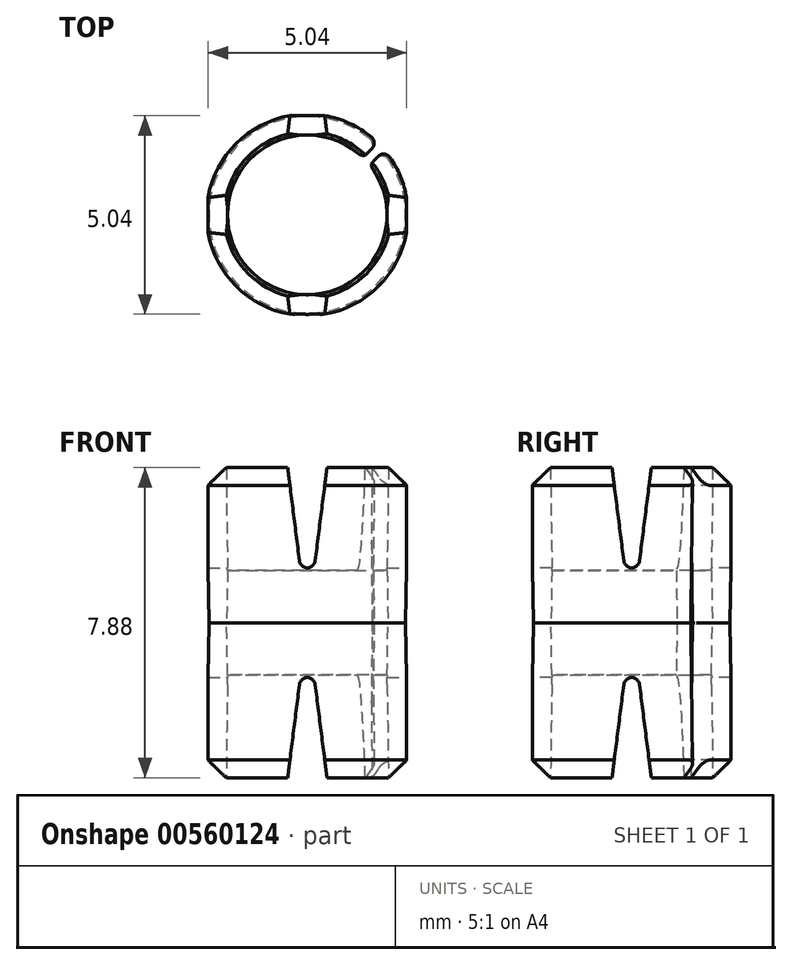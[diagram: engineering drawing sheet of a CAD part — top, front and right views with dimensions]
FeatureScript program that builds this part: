
annotation { "Feature Type Name" : "Feature", "Feature Type Description" : "" }
export const myFeature = defineFeature(function(context is Context, id is Id, definition is map)
    precondition{}
    {
        {
            var Q0;
            Q0=qCreatedBy(makeId("Top.planeOp"),FACE);
            var sketch = newSketch(context, id + "F0", { "sketchPlane" : qUnion([Q0])});
            skCircle(sketch, "E0", {"center": v(0, 0) * mm, "radius": 2.5 * mm});
            skCircle(sketch, "E1", {"center": v(0, 0) * mm, "radius": 2.05 * mm});
            skSolve(sketch);
        }
        {
            var Q0;
            Q0 = qSketchRegion(id + "F0", true);
            extrude(context, id + "F1", {"entities" : qUnion([Q0]), "depth" : 4 * mm, "offsetDistance" : 25 * mm, "hasDraft" : true, "draftAngle" : 1 * degree, "hasSecondDirection" : true, "secondDirectionOppositeDirection" : true, "secondDirectionDepth" : 4 * mm, "hasSecondDirectionDraft" : true, "secondDirectionDraftAngle" : 1 * degree});
        }
        {
            var Q0;
            Q0=qCreatedBy(makeId("Top.planeOp"),FACE);
            var sketch = newSketch(context, id + "F2", { "sketchPlane" : qUnion([Q0])});
            skCircle(sketch, "E2", {"center": v(0, 0) * mm, "radius": 1.98 * mm});
            skSolve(sketch);
        }
        {
            var Q0;
            Q0 = qSketchRegion(id + "F2", true);
            extrude(context, id + "F3", {"entities" : qUnion([Q0]), "operationType" : NewBodyOperationType.REMOVE, "endBound" : BoundingType.SYMMETRIC, "oppositeDirection" : true, "depth" : 50 * mm, "offsetDistance" : 25 * mm, "hasDraft" : true, "draftAngle" : 2 * degree});
        }
        {
            var Q0;
            Q0=makeQuery(id+"F1.opExtrude","CAP_EDGE",EDGE,{"disambiguationData":[OSD([sQuery(id+"F0.wireOp",EDGE,"E0")])],"isStart":false});
            var Q1;
            Q1=makeQuery(id+"F1.opExtrude","CAP_EDGE",EDGE,{"disambiguationData":[OSD([sQuery(id+"F0.wireOp",EDGE,"E0")])],"isStart":true});
            chamfer(context, id + "F4", {"entities" : qUnion([Q0, Q1]), "width" : 0.5 * mm, "tangentPropagation" : true});
        }
        {
            var Q0;
            Q0=qCreatedBy(makeId("Right.planeOp"),FACE);
            var sketch = newSketch(context, id + "F5", { "sketchPlane" : qUnion([Q0])});
            skLineSegment(sketch, "E3", {"start": v(0.2, -1.57) * mm, "end": v(0.5, -3.95) * mm});
            skLineSegment(sketch, "E4", {"start": v(0.5, -3.95) * mm, "end": v(-0.5, -3.95) * mm});
            skLineSegment(sketch, "E5", {"start": v(-0.5, -3.95) * mm, "end": v(-0.2, -1.57) * mm});
            skPoint(sketch, "E6.visualSharp", {"position": v(0, 0) * mm});
            skArc(sketch, "E6.filletArc", {"start": v(0.2, -1.57) * mm, "mid": v(0, -1.4) * mm, "end": v(-0.2, -1.57) * mm});
            skArc(sketch, "E7.MirrorCS", {"start": v(0.2, 1.57) * mm, "mid": v(0, 1.4) * mm, "end": v(-0.2, 1.57) * mm});
            skLineSegment(sketch, "E8.MirrorCS", {"start": v(0.2, 1.57) * mm, "end": v(0.5, 3.95) * mm});
            skLineSegment(sketch, "E9.MirrorCS", {"start": v(0.5, 3.95) * mm, "end": v(-0.5, 3.95) * mm});
            skLineSegment(sketch, "E10.MirrorCS", {"start": v(-0.5, 3.95) * mm, "end": v(-0.2, 1.57) * mm});
            skSolve(sketch);
        }
        {
            var Q0;
            Q0 = qSketchRegion(id + "F5", true);
            extrude(context, id + "F6", {"entities" : qUnion([Q0]), "operationType" : NewBodyOperationType.REMOVE, "oppositeDirection" : true, "depth" : 25 * mm, "offsetDistance" : 25 * mm, "hasSecondDirection" : true, "secondDirectionOppositeDirection" : false, "secondDirectionDepth" : 25 * mm});
        }
        {
            var Q0;
            Q0=qCreatedBy(makeId("Front.planeOp"),FACE);
            var sketch = newSketch(context, id + "F7", { "sketchPlane" : qUnion([Q0])});
            skLineSegment(sketch, "E11", {"start": v(0.2, -1.57) * mm, "end": v(0.5, -3.95) * mm});
            skLineSegment(sketch, "E12", {"start": v(0.5, -3.95) * mm, "end": v(-0.5, -3.95) * mm});
            skLineSegment(sketch, "E13", {"start": v(-0.5, -3.95) * mm, "end": v(-0.2, -1.57) * mm});
            skPoint(sketch, "E14.visualSharp", {"position": v(0, 0) * mm});
            skArc(sketch, "E14.filletArc", {"start": v(0.2, -1.57) * mm, "mid": v(0, -1.4) * mm, "end": v(-0.2, -1.57) * mm});
            skArc(sketch, "E15.MirrorCS", {"start": v(0.2, 1.57) * mm, "mid": v(0, 1.4) * mm, "end": v(-0.2, 1.57) * mm});
            skLineSegment(sketch, "E16.MirrorCS", {"start": v(0.2, 1.57) * mm, "end": v(0.5, 3.95) * mm});
            skLineSegment(sketch, "E17.MirrorCS", {"start": v(0.5, 3.95) * mm, "end": v(-0.5, 3.95) * mm});
            skLineSegment(sketch, "E18.MirrorCS", {"start": v(-0.5, 3.95) * mm, "end": v(-0.2, 1.57) * mm});
            skSolve(sketch);
        }
        {
            var Q0;
            Q0 = qSketchRegion(id + "F7", true);
            extrude(context, id + "F8", {"entities" : qUnion([Q0]), "operationType" : NewBodyOperationType.REMOVE, "oppositeDirection" : true, "depth" : 25 * mm, "offsetDistance" : 25 * mm, "hasSecondDirection" : true, "secondDirectionOppositeDirection" : false, "secondDirectionDepth" : 25 * mm});
        }
        {
            var Q0;
            Q0=qCreatedBy(makeId("Top.planeOp"),FACE);
            var sketch = newSketch(context, id + "F9", { "sketchPlane" : qUnion([Q0])});
            skLineSegment(sketch, "E19", {"start": v(0, 0) * mm, "end": v(3.4, 3.48) * mm});
            skLineSegment(sketch, "E20", {"start": v(3.4, 3.48) * mm, "end": v(3.57, 3.3) * mm});
            skLineSegment(sketch, "E21", {"start": v(3.57, 3.3) * mm, "end": v(0.56, 0.22) * mm});
            skLineSegment(sketch, "E22", {"start": v(0.56, 0.22) * mm, "end": v(0, 0) * mm});
            skSolve(sketch);
        }
        {
            var Q0;
            Q0=makeQuery(id+"F9.imprint","IMPRINT",FACE,{"disambiguationData":[TD([[makeQuery(id+"F9.imprint","IMPRINT",EDGE,{"derivedFrom":sQuery(id+"F9.wireOp",EDGE,"E19")}),-1.0]])]});
            extrude(context, id + "F10", {"entities" : qUnion([Q0]), "operationType" : NewBodyOperationType.REMOVE, "depth" : 25 * mm, "offsetDistance" : 25 * mm, "hasSecondDirection" : true, "secondDirectionOppositeDirection" : true, "secondDirectionDepth" : 25 * mm});
        }
        {
            var Q0;
            Q0=makeQuery(id+"F10.boolean.opBoolean","INTERSECT",EDGE,{"derivedFrom":[makeQuery(id+"F1.*.split.splitOp","SPLIT",FACE,{"derivedFrom":makeQuery(id+"F1.opExtrude","SWEPT_FACE",FACE,{"disambiguationData":[OSD([sQuery(id+"F0.wireOp",EDGE,"E1")])]})}),makeQuery(id+"F10.opExtrude","SWEPT_FACE",FACE,{"disambiguationData":[OSD([sQuery(id+"F9.wireOp",EDGE,"E19")])]})]});
            var Q1;
            Q1=makeQuery(id+"F10.boolean.opBoolean","INTERSECT",EDGE,{"derivedFrom":[makeQuery(id+"F1.*.split.splitOp","SPLIT",FACE,{"derivedFrom":makeQuery(id+"F1.opExtrude","SWEPT_FACE",FACE,{"disambiguationData":[OSD([sQuery(id+"F0.wireOp",EDGE,"E1")])]}),"isFromBackBody":true}),makeQuery(id+"F10.opExtrude","SWEPT_FACE",FACE,{"disambiguationData":[OSD([sQuery(id+"F9.wireOp",EDGE,"E19")])]})]});
            var Q2;
            Q2=makeQuery(id+"F10.boolean.opBoolean","INTERSECT",EDGE,{"derivedFrom":[makeQuery(id+"F1.*.split.splitOp","SPLIT",FACE,{"derivedFrom":makeQuery(id+"F1.opExtrude","SWEPT_FACE",FACE,{"disambiguationData":[OSD([sQuery(id+"F0.wireOp",EDGE,"E1")])]}),"isFromBackBody":true}),makeQuery(id+"F10.opExtrude","SWEPT_FACE",FACE,{"disambiguationData":[OSD([sQuery(id+"F9.wireOp",EDGE,"E21")])]})]});
            var Q3;
            Q3=makeQuery(id+"F10.boolean.opBoolean","INTERSECT",EDGE,{"derivedFrom":[makeQuery(id+"F1.*.split.splitOp","SPLIT",FACE,{"derivedFrom":makeQuery(id+"F1.opExtrude","SWEPT_FACE",FACE,{"disambiguationData":[OSD([sQuery(id+"F0.wireOp",EDGE,"E1")])]})}),makeQuery(id+"F10.opExtrude","SWEPT_FACE",FACE,{"disambiguationData":[OSD([sQuery(id+"F9.wireOp",EDGE,"E21")])]})]});
            var Q4;
            Q4=makeQuery(id+"F10.boolean.opBoolean","INTERSECT",EDGE,{"derivedFrom":[makeQuery(id+"F1.*.split.splitOp","SPLIT",FACE,{"derivedFrom":makeQuery(id+"F1.opExtrude","SWEPT_FACE",FACE,{"disambiguationData":[OSD([sQuery(id+"F0.wireOp",EDGE,"E0")])]}),"isFromBackBody":true}),makeQuery(id+"F10.opExtrude","SWEPT_FACE",FACE,{"disambiguationData":[OSD([sQuery(id+"F9.wireOp",EDGE,"E21")])]})]});
            var Q5;
            Q5=makeQuery(id+"F10.boolean.opBoolean","INTERSECT",EDGE,{"derivedFrom":[makeQuery(id+"F1.*.split.splitOp","SPLIT",FACE,{"derivedFrom":makeQuery(id+"F1.opExtrude","SWEPT_FACE",FACE,{"disambiguationData":[OSD([sQuery(id+"F0.wireOp",EDGE,"E0")])]})}),makeQuery(id+"F10.opExtrude","SWEPT_FACE",FACE,{"disambiguationData":[OSD([sQuery(id+"F9.wireOp",EDGE,"E21")])]})]});
            var Q6;
            Q6=makeQuery(id+"F10.boolean.opBoolean","INTERSECT",EDGE,{"derivedFrom":[makeQuery(id+"F1.*.split.splitOp","SPLIT",FACE,{"derivedFrom":makeQuery(id+"F1.opExtrude","SWEPT_FACE",FACE,{"disambiguationData":[OSD([sQuery(id+"F0.wireOp",EDGE,"E0")])]})}),makeQuery(id+"F10.opExtrude","SWEPT_FACE",FACE,{"disambiguationData":[OSD([sQuery(id+"F9.wireOp",EDGE,"E19")])]})]});
            var Q7;
            Q7=makeQuery(id+"F10.boolean.opBoolean","INTERSECT",EDGE,{"derivedFrom":[makeQuery(id+"F1.*.split.splitOp","SPLIT",FACE,{"derivedFrom":makeQuery(id+"F1.opExtrude","SWEPT_FACE",FACE,{"disambiguationData":[OSD([sQuery(id+"F0.wireOp",EDGE,"E0")])]}),"isFromBackBody":true}),makeQuery(id+"F10.opExtrude","SWEPT_FACE",FACE,{"disambiguationData":[OSD([sQuery(id+"F9.wireOp",EDGE,"E19")])]})]});
            fillet(context, id + "F11", {"entities" : qUnion([Q0, Q1, Q2, Q3, Q4, Q5, Q6, Q7]), "radius" : 0.2 * mm, "tangentPropagation" : true, "allowEdgeOverflow" : false});
        }
    });
